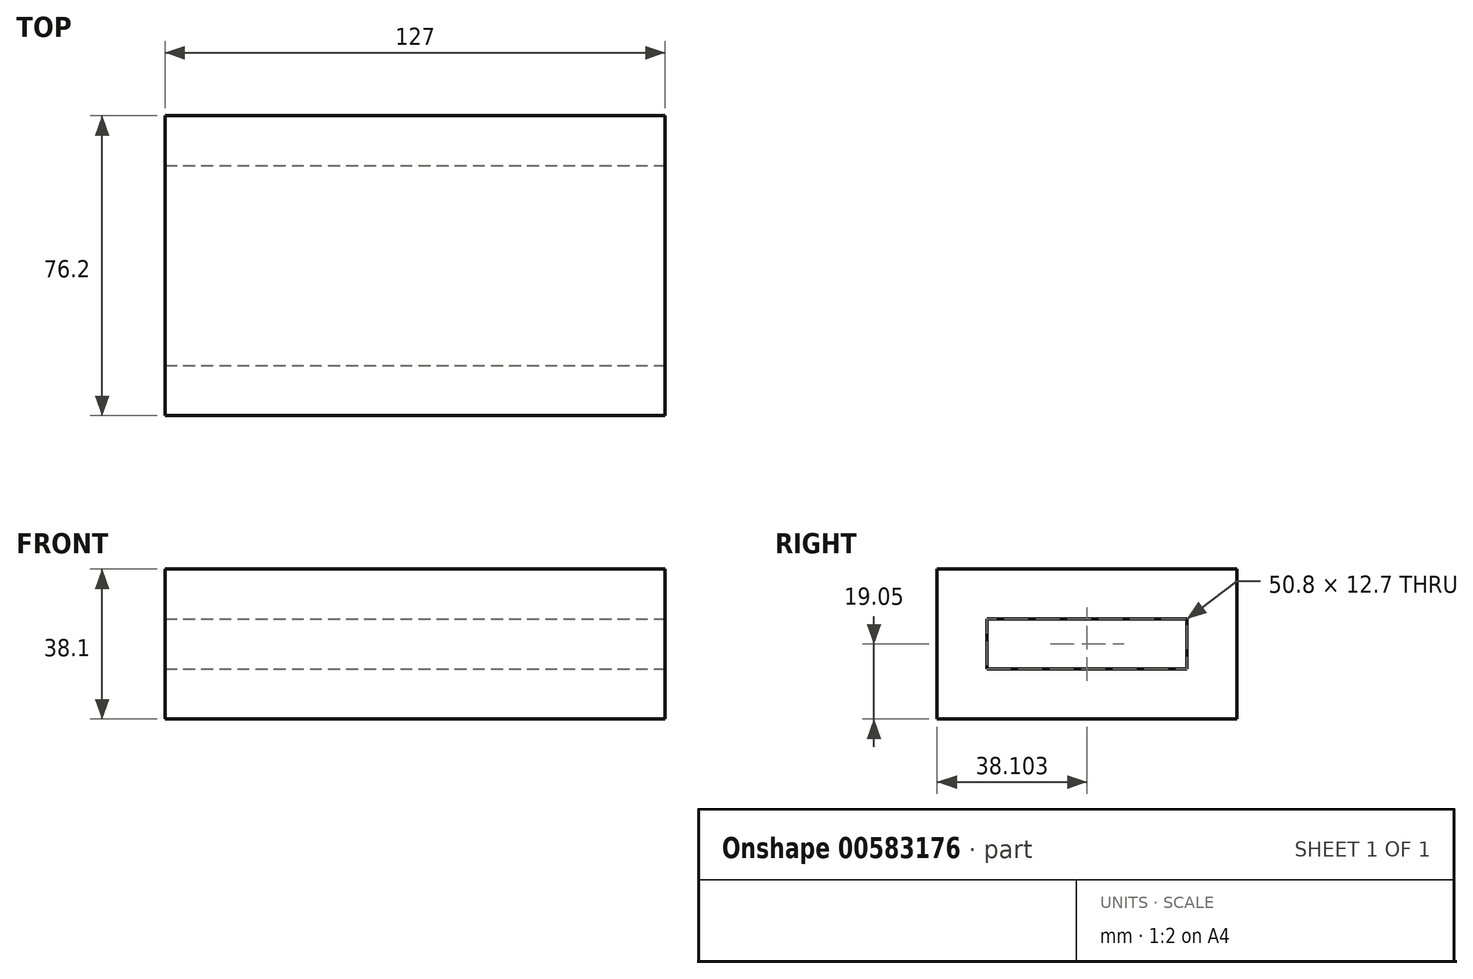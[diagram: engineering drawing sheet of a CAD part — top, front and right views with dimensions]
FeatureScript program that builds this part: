
annotation { "Feature Type Name" : "Feature", "Feature Type Description" : "" }
export const myFeature = defineFeature(function(context is Context, id is Id, definition is map)
    precondition{}
    {
        {
            var Q0;
            Q0=qCreatedBy(makeId("Top.planeOp"),FACE);
            var sketch = newSketch(context, id + "F0", { "sketchPlane" : qUnion([Q0])});
            skLineSegment(sketch, "E0.bottom", {"start": v(-109.77, 79.45) * mm, "end": v(17.23, 79.45) * mm});
            skLineSegment(sketch, "E0.top", {"start": v(-109.77, 3.25) * mm, "end": v(17.23, 3.25) * mm});
            skLineSegment(sketch, "E0.left", {"start": v(-109.77, 79.45) * mm, "end": v(-109.77, 3.25) * mm});
            skLineSegment(sketch, "E0.right", {"start": v(17.23, 79.45) * mm, "end": v(17.23, 3.25) * mm});
            skSolve(sketch);
        }
        {
            var Q0;
            Q0 = qSketchRegion(id + "F0", true);
            extrude(context, id + "F1", {"entities" : qUnion([Q0]), "depth" : 12.7 * mm, "offsetDistance" : 25.4 * mm});
        }
        {
            var Q0;
            Q0=makeQuery(id+"F1.opExtrude","CAP_FACE",FACE,{"disambiguationData":[OSD([sQuery(id+"F0.wireOp",EDGE,"E0.bottom"),sQuery(id+"F0.wireOp",EDGE,"E0.top"),sQuery(id+"F0.wireOp",EDGE,"E0.left"),sQuery(id+"F0.wireOp",EDGE,"E0.right")])],"isStart":false});
            var sketch = newSketch(context, id + "F2", { "sketchPlane" : qUnion([Q0])});
            skLineSegment(sketch, "E1.bottom", {"start": v(-109.77, 3.25) * mm, "end": v(17.23, 3.25) * mm});
            skLineSegment(sketch, "E1.top", {"start": v(-109.77, 15.95) * mm, "end": v(17.23, 15.95) * mm});
            skLineSegment(sketch, "E1.left", {"start": v(-109.77, 3.25) * mm, "end": v(-109.77, 15.95) * mm});
            skLineSegment(sketch, "E1.right", {"start": v(17.23, 3.25) * mm, "end": v(17.23, 15.95) * mm});
            skSolve(sketch);
        }
        {
            var Q0;
            Q0 = qSketchRegion(id + "F2", true);
            extrude(context, id + "F3", {"entities" : qUnion([Q0]), "operationType" : NewBodyOperationType.ADD, "depth" : 12.7 * mm, "offsetDistance" : 25.4 * mm});
        }
        {
            var Q0;
            Q0=makeQuery(id+"F1.opExtrude","CAP_FACE",FACE,{"disambiguationData":[OSD([sQuery(id+"F0.wireOp",EDGE,"E0.bottom"),sQuery(id+"F0.wireOp",EDGE,"E0.top"),sQuery(id+"F0.wireOp",EDGE,"E0.left"),sQuery(id+"F0.wireOp",EDGE,"E0.right")])],"isStart":false});
            var sketch = newSketch(context, id + "F4", { "sketchPlane" : qUnion([Q0])});
            skLineSegment(sketch, "E2.bottom", {"start": v(-109.77, 79.45) * mm, "end": v(17.23, 79.45) * mm});
            skLineSegment(sketch, "E2.top", {"start": v(-109.77, 66.75) * mm, "end": v(17.23, 66.75) * mm});
            skLineSegment(sketch, "E2.left", {"start": v(-109.77, 79.45) * mm, "end": v(-109.77, 66.75) * mm});
            skLineSegment(sketch, "E2.right", {"start": v(17.23, 79.45) * mm, "end": v(17.23, 66.75) * mm});
            skSolve(sketch);
        }
        {
            var Q0;
            Q0 = qSketchRegion(id + "F4", true);
            extrude(context, id + "F5", {"entities" : qUnion([Q0]), "operationType" : NewBodyOperationType.ADD, "depth" : 12.7 * mm, "offsetDistance" : 25.4 * mm});
        }
        {
            var Q0;
            Q0=makeQuery(id+"F5.opExtrude","CAP_FACE",FACE,{"disambiguationData":[OSD([sQuery(id+"F4.wireOp",EDGE,"E2.bottom"),sQuery(id+"F4.wireOp",EDGE,"E2.top"),sQuery(id+"F4.wireOp",EDGE,"E2.left"),sQuery(id+"F4.wireOp",EDGE,"E2.right")])],"isStart":false});
            var sketch = newSketch(context, id + "F6", { "sketchPlane" : qUnion([Q0])});
            skLineSegment(sketch, "E3.bottom", {"start": v(-109.77, 79.45) * mm, "end": v(17.23, 79.45) * mm});
            skLineSegment(sketch, "E3.top", {"start": v(-109.77, 3.25) * mm, "end": v(17.23, 3.25) * mm});
            skLineSegment(sketch, "E3.left", {"start": v(-109.77, 79.45) * mm, "end": v(-109.77, 3.25) * mm});
            skLineSegment(sketch, "E3.right", {"start": v(17.23, 79.45) * mm, "end": v(17.23, 3.25) * mm});
            skSolve(sketch);
        }
        {
            var Q0;
            Q0 = qSketchRegion(id + "F6", true);
            extrude(context, id + "F7", {"entities" : qUnion([Q0]), "operationType" : NewBodyOperationType.ADD, "depth" : 12.7 * mm, "offsetDistance" : 25.4 * mm});
        }
    });
